# Revit family: Folding_Shower_Dressing_Area_Seat-Bobrick-819687
name_source: partatom
category: Specialty Equipment
revit_build: Autodesk Revit 2018 (Build: 20170223_1515(x64)
units: mm (PartAtom-declared; Revit-internal decimal feet)

## family parameters
Cut with Voids When Loaded = No
Host = Face
OmniClass Number = 23.40.20.00
OmniClass Title = General Furniture and Specialties
Part Type = Normal
Room Calculation Point = No
Round Connector Dimension = Use Diameter
Shared = Yes

## types (1)
- 819687
    ADA Compliant = Yes
    ADA Height (17" to 19") = 19"
    Assembly Code = E1010
    CW Connection = No
    Default Elevation = 19"
    Description = Folding seat of one-piece, 13 mm thick solid phenolic, ivory-colored face. Integral holes for water drainage.
    HW Connection = No
    Installation Type = Wall
    Manufacturer = Bobrick
    Model = 819687
    Price = Prices may vary. Please consult Manufacturer Representative for most up-to-date price list.
    Product Documentation Link = https://www.bobrick.com
    Product Page URL = https://www.bobrick.com
    URL = https://www.bobrick.com
    Vent Connection = No
    Waste Connection = No

## geometry (parser evidence)
native form markers: Sweep x5
no freeform markers — native parametric forms only
